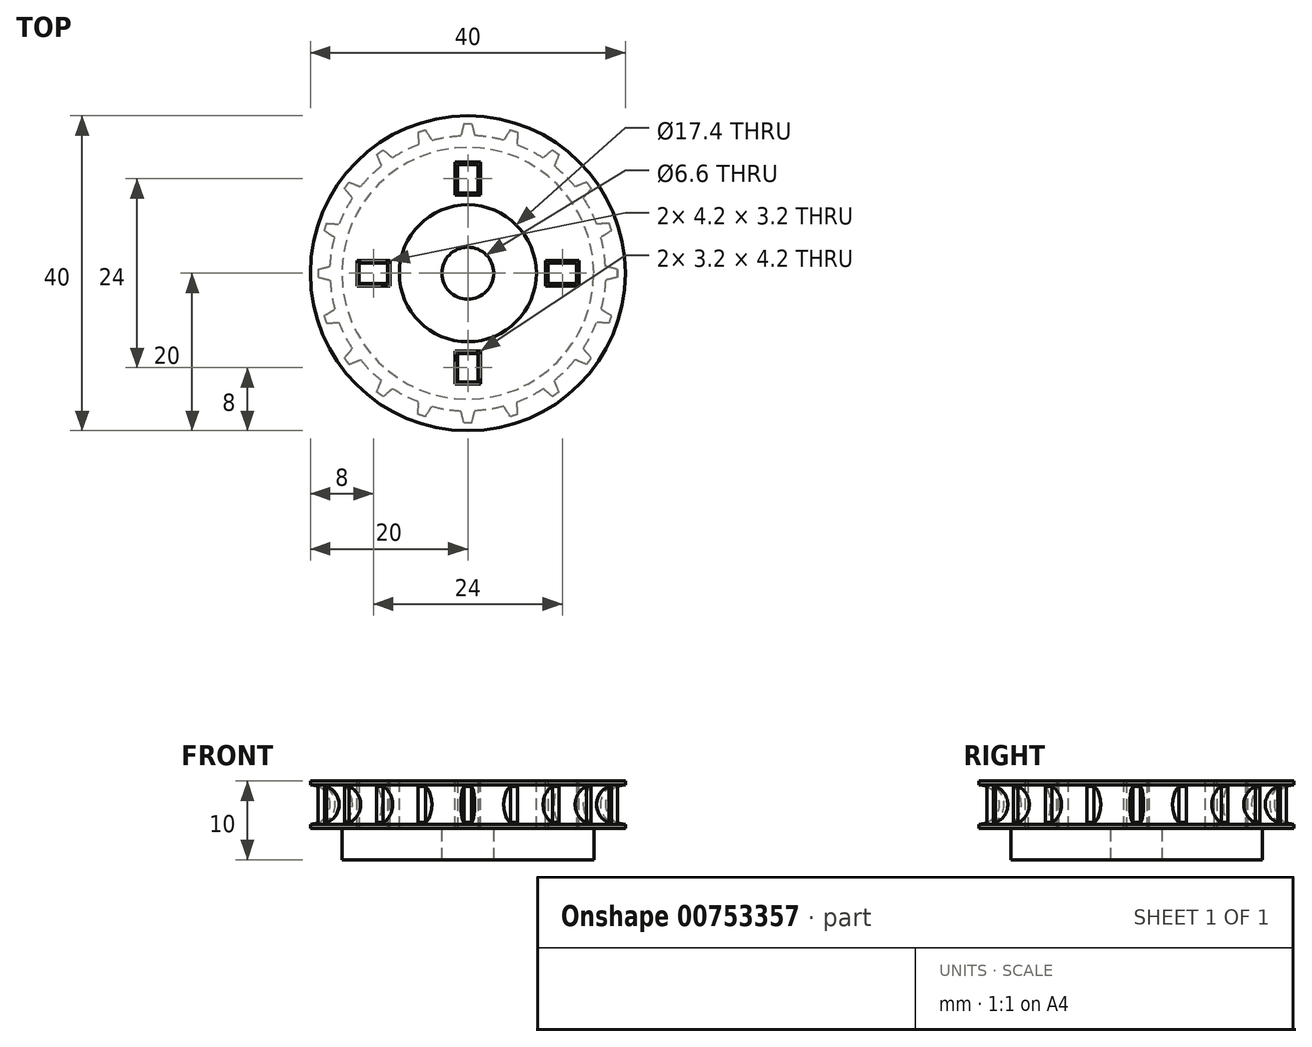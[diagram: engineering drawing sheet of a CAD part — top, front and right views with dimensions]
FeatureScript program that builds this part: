
annotation { "Feature Type Name" : "Feature", "Feature Type Description" : "" }
export const myFeature = defineFeature(function(context is Context, id is Id, definition is map)
    precondition{}
    {
        {
            var Q0;
            Q0=qCreatedBy(makeId("Right.planeOp"),FACE);
            var sketch = newSketch(context, id + "F0", { "sketchPlane" : qUnion([Q0])});
            skLineSegment(sketch, "E0", {"start": v(0, 6) * mm, "end": v(-20, 6) * mm});
            skLineSegment(sketch, "E1", {"start": v(-20, 5.5) * mm, "end": v(-20, 6) * mm});
            skLineSegment(sketch, "E2", {"start": v(-20, 0.5) * mm, "end": v(-20, 0) * mm});
            skArc(sketch, "E3", {"start": v(-20, 0.5) * mm, "mid": v(-17.5, 3) * mm, "end": v(-20, 5.5) * mm});
            skLineSegment(sketch, "E4", {"start": v(0, 6) * mm, "end": v(0, 0) * mm});
            skLineSegment(sketch, "E5", {"start": v(0, -4) * mm, "end": v(0, 0) * mm});
            skLineSegment(sketch, "E6", {"start": v(0, -4) * mm, "end": v(-16, -4) * mm});
            skLineSegment(sketch, "E7", {"start": v(-16, -4) * mm, "end": v(-16, 0) * mm});
            skLineSegment(sketch, "E8", {"start": v(-16, 0) * mm, "end": v(-20, 0) * mm});
            skLineSegment(sketch, "E9", {"start": v(-16, 0) * mm, "end": v(0, 0) * mm});
            skSolve(sketch);
        }
        {
            var Q0;
            Q0=makeQuery(id+"F0.imprint","IMPRINT",FACE,{"disambiguationData":[TD([[makeQuery(id+"F0.imprint","IMPRINT",EDGE,{"derivedFrom":sQuery(id+"F0.wireOp",EDGE,"E0")}),1.0]])]});
            var Q1;
            Q1=sQuery(id+"F0.wireOp",EDGE,"E4");
            revolve(context, id + "F1", {"surfaceOperationType" : NewSurfaceOperationType.NEW, "entities" : qUnion([Q0]), "axis" : qUnion([Q1]), "revolveType" : RevolveType.FULL});
        }
        {
            var Q0;
            Q0=makeQuery(id+"F1.opRevolve","SWEPT_FACE",FACE,{"disambiguationData":[OSD([sQuery(id+"F0.wireOp",EDGE,"E0")])]});
            var sketch = newSketch(context, id + "F2", { "sketchPlane" : qUnion([Q0])});
            skLineSegment(sketch, "E10", {"start": v(-17, 1) * mm, "end": v(-17, 0) * mm});
            skLineSegment(sketch, "E11", {"start": v(-17, 0) * mm, "end": v(-17, -1) * mm});
            skLineSegment(sketch, "E12", {"start": v(-17, -1) * mm, "end": v(-19, -0.5) * mm});
            skLineSegment(sketch, "E13", {"start": v(-19, -0.5) * mm, "end": v(-19, 0.5) * mm});
            skLineSegment(sketch, "E14", {"start": v(-19, 0.5) * mm, "end": v(-17, 1) * mm});
            skPoint(sketch, "E15", {"position": v(0, 0) * mm});
            skLineSegment(sketch, "E16", {"start": v(0, 9.9) * mm, "end": v(1.6, 9.9) * mm});
            skLineSegment(sketch, "E17", {"start": v(1.6, 9.9) * mm, "end": v(1.6, 14.1) * mm});
            skLineSegment(sketch, "E18", {"start": v(1.6, 14.1) * mm, "end": v(-1.6, 14.1) * mm});
            skLineSegment(sketch, "E19", {"start": v(0, 9.9) * mm, "end": v(-1.6, 9.9) * mm});
            skLineSegment(sketch, "E20", {"start": v(-1.6, 9.9) * mm, "end": v(-1.6, 14.1) * mm});
            skLineSegment(sketch, "E21.1.0", {"start": v(-18.22, -5.4) * mm, "end": v(-16.48, -4.3) * mm});
            skLineSegment(sketch, "E21.1.1", {"start": v(-15.86, -6.2) * mm, "end": v(-17.92, -6.35) * mm});
            skLineSegment(sketch, "E21.1.2", {"start": v(-17.92, -6.35) * mm, "end": v(-18.22, -5.4) * mm});
            skLineSegment(sketch, "E21.1.3", {"start": v(-16.17, -5.25) * mm, "end": v(-15.86, -6.2) * mm});
            skLineSegment(sketch, "E21.1.4", {"start": v(-16.48, -4.3) * mm, "end": v(-16.17, -5.25) * mm});
            skLineSegment(sketch, "E21.2.0", {"start": v(-15.67, -10.76) * mm, "end": v(-14.34, -9.18) * mm});
            skLineSegment(sketch, "E21.2.1", {"start": v(-13.17, -10.8) * mm, "end": v(-15.08, -11.57) * mm});
            skLineSegment(sketch, "E21.2.2", {"start": v(-15.08, -11.57) * mm, "end": v(-15.67, -10.76) * mm});
            skLineSegment(sketch, "E21.2.3", {"start": v(-13.75, -10) * mm, "end": v(-13.17, -10.8) * mm});
            skLineSegment(sketch, "E21.2.4", {"start": v(-14.34, -9.18) * mm, "end": v(-13.75, -10) * mm});
            skLineSegment(sketch, "E21.3.0", {"start": v(-11.57, -15.08) * mm, "end": v(-10.8, -13.17) * mm});
            skLineSegment(sketch, "E21.3.1", {"start": v(-9.18, -14.34) * mm, "end": v(-10.76, -15.67) * mm});
            skLineSegment(sketch, "E21.3.2", {"start": v(-10.76, -15.67) * mm, "end": v(-11.57, -15.08) * mm});
            skLineSegment(sketch, "E21.3.3", {"start": v(-10, -13.75) * mm, "end": v(-9.18, -14.34) * mm});
            skLineSegment(sketch, "E21.3.4", {"start": v(-10.8, -13.17) * mm, "end": v(-10, -13.75) * mm});
            skLineSegment(sketch, "E21.4.0", {"start": v(-6.35, -17.92) * mm, "end": v(-6.2, -15.86) * mm});
            skLineSegment(sketch, "E21.4.1", {"start": v(-4.3, -16.48) * mm, "end": v(-5.4, -18.22) * mm});
            skLineSegment(sketch, "E21.4.2", {"start": v(-5.4, -18.22) * mm, "end": v(-6.35, -17.92) * mm});
            skLineSegment(sketch, "E21.4.3", {"start": v(-5.25, -16.17) * mm, "end": v(-4.3, -16.48) * mm});
            skLineSegment(sketch, "E21.4.4", {"start": v(-6.2, -15.86) * mm, "end": v(-5.25, -16.17) * mm});
            skLineSegment(sketch, "E21.5.0", {"start": v(-0.5, -19) * mm, "end": v(-1, -17) * mm});
            skLineSegment(sketch, "E21.5.1", {"start": v(1, -17) * mm, "end": v(0.5, -19) * mm});
            skLineSegment(sketch, "E21.5.2", {"start": v(0.5, -19) * mm, "end": v(-0.5, -19) * mm});
            skLineSegment(sketch, "E21.5.3", {"start": v(0, -17) * mm, "end": v(1, -17) * mm});
            skLineSegment(sketch, "E21.5.4", {"start": v(-1, -17) * mm, "end": v(0, -17) * mm});
            skLineSegment(sketch, "E21.6.0", {"start": v(5.4, -18.22) * mm, "end": v(4.3, -16.48) * mm});
            skLineSegment(sketch, "E21.6.1", {"start": v(6.2, -15.86) * mm, "end": v(6.35, -17.92) * mm});
            skLineSegment(sketch, "E21.6.2", {"start": v(6.35, -17.92) * mm, "end": v(5.4, -18.22) * mm});
            skLineSegment(sketch, "E21.6.3", {"start": v(5.25, -16.17) * mm, "end": v(6.2, -15.86) * mm});
            skLineSegment(sketch, "E21.6.4", {"start": v(4.3, -16.48) * mm, "end": v(5.25, -16.17) * mm});
            skLineSegment(sketch, "E21.7.0", {"start": v(10.76, -15.67) * mm, "end": v(9.18, -14.34) * mm});
            skLineSegment(sketch, "E21.7.1", {"start": v(10.8, -13.17) * mm, "end": v(11.57, -15.08) * mm});
            skLineSegment(sketch, "E21.7.2", {"start": v(11.57, -15.08) * mm, "end": v(10.76, -15.67) * mm});
            skLineSegment(sketch, "E21.7.3", {"start": v(10, -13.75) * mm, "end": v(10.8, -13.17) * mm});
            skLineSegment(sketch, "E21.7.4", {"start": v(9.18, -14.34) * mm, "end": v(10, -13.75) * mm});
            skLineSegment(sketch, "E21.8.0", {"start": v(15.08, -11.57) * mm, "end": v(13.17, -10.8) * mm});
            skLineSegment(sketch, "E21.8.1", {"start": v(14.34, -9.18) * mm, "end": v(15.67, -10.76) * mm});
            skLineSegment(sketch, "E21.8.2", {"start": v(15.67, -10.76) * mm, "end": v(15.08, -11.57) * mm});
            skLineSegment(sketch, "E21.8.3", {"start": v(13.75, -10) * mm, "end": v(14.34, -9.18) * mm});
            skLineSegment(sketch, "E21.8.4", {"start": v(13.17, -10.8) * mm, "end": v(13.75, -10) * mm});
            skLineSegment(sketch, "E21.9.0", {"start": v(17.92, -6.35) * mm, "end": v(15.86, -6.2) * mm});
            skLineSegment(sketch, "E21.9.1", {"start": v(16.48, -4.3) * mm, "end": v(18.22, -5.4) * mm});
            skLineSegment(sketch, "E21.9.2", {"start": v(18.22, -5.4) * mm, "end": v(17.92, -6.35) * mm});
            skLineSegment(sketch, "E21.9.3", {"start": v(16.17, -5.25) * mm, "end": v(16.48, -4.3) * mm});
            skLineSegment(sketch, "E21.9.4", {"start": v(15.86, -6.2) * mm, "end": v(16.17, -5.25) * mm});
            skLineSegment(sketch, "E21.10.0", {"start": v(19, -0.5) * mm, "end": v(17, -1) * mm});
            skLineSegment(sketch, "E21.10.1", {"start": v(17, 1) * mm, "end": v(19, 0.5) * mm});
            skLineSegment(sketch, "E21.10.2", {"start": v(19, 0.5) * mm, "end": v(19, -0.5) * mm});
            skLineSegment(sketch, "E21.10.3", {"start": v(17, 0) * mm, "end": v(17, 1) * mm});
            skLineSegment(sketch, "E21.10.4", {"start": v(17, -1) * mm, "end": v(17, 0) * mm});
            skLineSegment(sketch, "E21.11.0", {"start": v(18.22, 5.4) * mm, "end": v(16.48, 4.3) * mm});
            skLineSegment(sketch, "E21.11.1", {"start": v(15.86, 6.2) * mm, "end": v(17.92, 6.35) * mm});
            skLineSegment(sketch, "E21.11.2", {"start": v(17.92, 6.35) * mm, "end": v(18.22, 5.4) * mm});
            skLineSegment(sketch, "E21.11.3", {"start": v(16.17, 5.25) * mm, "end": v(15.86, 6.2) * mm});
            skLineSegment(sketch, "E21.11.4", {"start": v(16.48, 4.3) * mm, "end": v(16.17, 5.25) * mm});
            skLineSegment(sketch, "E21.12.0", {"start": v(15.67, 10.76) * mm, "end": v(14.34, 9.18) * mm});
            skLineSegment(sketch, "E21.12.1", {"start": v(13.17, 10.8) * mm, "end": v(15.08, 11.57) * mm});
            skLineSegment(sketch, "E21.12.2", {"start": v(15.08, 11.57) * mm, "end": v(15.67, 10.76) * mm});
            skLineSegment(sketch, "E21.12.3", {"start": v(13.75, 10) * mm, "end": v(13.17, 10.8) * mm});
            skLineSegment(sketch, "E21.12.4", {"start": v(14.34, 9.18) * mm, "end": v(13.75, 10) * mm});
            skLineSegment(sketch, "E21.13.0", {"start": v(11.57, 15.08) * mm, "end": v(10.8, 13.17) * mm});
            skLineSegment(sketch, "E21.13.1", {"start": v(9.18, 14.34) * mm, "end": v(10.76, 15.67) * mm});
            skLineSegment(sketch, "E21.13.2", {"start": v(10.76, 15.67) * mm, "end": v(11.57, 15.08) * mm});
            skLineSegment(sketch, "E21.13.3", {"start": v(10, 13.75) * mm, "end": v(9.18, 14.34) * mm});
            skLineSegment(sketch, "E21.13.4", {"start": v(10.8, 13.17) * mm, "end": v(10, 13.75) * mm});
            skLineSegment(sketch, "E21.14.0", {"start": v(6.35, 17.92) * mm, "end": v(6.2, 15.86) * mm});
            skLineSegment(sketch, "E21.14.1", {"start": v(4.3, 16.48) * mm, "end": v(5.4, 18.22) * mm});
            skLineSegment(sketch, "E21.14.2", {"start": v(5.4, 18.22) * mm, "end": v(6.35, 17.92) * mm});
            skLineSegment(sketch, "E21.14.3", {"start": v(5.25, 16.17) * mm, "end": v(4.3, 16.48) * mm});
            skLineSegment(sketch, "E21.14.4", {"start": v(6.2, 15.86) * mm, "end": v(5.25, 16.17) * mm});
            skLineSegment(sketch, "E21.15.0", {"start": v(0.5, 19) * mm, "end": v(1, 17) * mm});
            skLineSegment(sketch, "E21.15.1", {"start": v(-1, 17) * mm, "end": v(-0.5, 19) * mm});
            skLineSegment(sketch, "E21.15.2", {"start": v(-0.5, 19) * mm, "end": v(0.5, 19) * mm});
            skLineSegment(sketch, "E21.15.3", {"start": v(0, 17) * mm, "end": v(-1, 17) * mm});
            skLineSegment(sketch, "E21.15.4", {"start": v(1, 17) * mm, "end": v(0, 17) * mm});
            skLineSegment(sketch, "E21.16.0", {"start": v(-5.4, 18.22) * mm, "end": v(-4.3, 16.48) * mm});
            skLineSegment(sketch, "E21.16.1", {"start": v(-6.2, 15.86) * mm, "end": v(-6.35, 17.92) * mm});
            skLineSegment(sketch, "E21.16.2", {"start": v(-6.35, 17.92) * mm, "end": v(-5.4, 18.22) * mm});
            skLineSegment(sketch, "E21.16.3", {"start": v(-5.25, 16.17) * mm, "end": v(-6.2, 15.86) * mm});
            skLineSegment(sketch, "E21.16.4", {"start": v(-4.3, 16.48) * mm, "end": v(-5.25, 16.17) * mm});
            skLineSegment(sketch, "E21.17.0", {"start": v(-10.76, 15.67) * mm, "end": v(-9.18, 14.34) * mm});
            skLineSegment(sketch, "E21.17.1", {"start": v(-10.8, 13.17) * mm, "end": v(-11.57, 15.08) * mm});
            skLineSegment(sketch, "E21.17.2", {"start": v(-11.57, 15.08) * mm, "end": v(-10.76, 15.67) * mm});
            skLineSegment(sketch, "E21.17.3", {"start": v(-10, 13.75) * mm, "end": v(-10.8, 13.17) * mm});
            skLineSegment(sketch, "E21.17.4", {"start": v(-9.18, 14.34) * mm, "end": v(-10, 13.75) * mm});
            skLineSegment(sketch, "E21.18.0", {"start": v(-15.08, 11.57) * mm, "end": v(-13.17, 10.8) * mm});
            skLineSegment(sketch, "E21.18.1", {"start": v(-14.34, 9.18) * mm, "end": v(-15.67, 10.76) * mm});
            skLineSegment(sketch, "E21.18.2", {"start": v(-15.67, 10.76) * mm, "end": v(-15.08, 11.57) * mm});
            skLineSegment(sketch, "E21.18.3", {"start": v(-13.75, 10) * mm, "end": v(-14.34, 9.18) * mm});
            skLineSegment(sketch, "E21.18.4", {"start": v(-13.17, 10.8) * mm, "end": v(-13.75, 10) * mm});
            skLineSegment(sketch, "E21.19.0", {"start": v(-17.92, 6.35) * mm, "end": v(-15.86, 6.2) * mm});
            skLineSegment(sketch, "E21.19.1", {"start": v(-16.48, 4.3) * mm, "end": v(-18.22, 5.4) * mm});
            skLineSegment(sketch, "E21.19.2", {"start": v(-18.22, 5.4) * mm, "end": v(-17.92, 6.35) * mm});
            skLineSegment(sketch, "E21.19.3", {"start": v(-16.17, 5.25) * mm, "end": v(-16.48, 4.3) * mm});
            skLineSegment(sketch, "E21.19.4", {"start": v(-15.86, 6.2) * mm, "end": v(-16.17, 5.25) * mm});
            skPoint(sketch, "E22.center", {"position": v(0.05, 0.05) * mm});
            skLineSegment(sketch, "E23.1.0", {"start": v(-9.9, 0) * mm, "end": v(-9.9, 1.6) * mm});
            skLineSegment(sketch, "E23.1.1", {"start": v(-9.9, 1.6) * mm, "end": v(-14.1, 1.6) * mm});
            skLineSegment(sketch, "E23.1.2", {"start": v(-9.9, -1.6) * mm, "end": v(-14.1, -1.6) * mm});
            skLineSegment(sketch, "E23.1.3", {"start": v(-9.9, 0) * mm, "end": v(-9.9, -1.6) * mm});
            skLineSegment(sketch, "E23.1.4", {"start": v(-14.1, 1.6) * mm, "end": v(-14.1, -1.6) * mm});
            skLineSegment(sketch, "E23.2.0", {"start": v(0, -9.9) * mm, "end": v(-1.6, -9.9) * mm});
            skLineSegment(sketch, "E23.2.1", {"start": v(-1.6, -9.9) * mm, "end": v(-1.6, -14.1) * mm});
            skLineSegment(sketch, "E23.2.2", {"start": v(1.6, -9.9) * mm, "end": v(1.6, -14.1) * mm});
            skLineSegment(sketch, "E23.2.3", {"start": v(0, -9.9) * mm, "end": v(1.6, -9.9) * mm});
            skLineSegment(sketch, "E23.2.4", {"start": v(-1.6, -14.1) * mm, "end": v(1.6, -14.1) * mm});
            skLineSegment(sketch, "E23.3.0", {"start": v(9.9, 0) * mm, "end": v(9.9, -1.6) * mm});
            skLineSegment(sketch, "E23.3.1", {"start": v(9.9, -1.6) * mm, "end": v(14.1, -1.6) * mm});
            skLineSegment(sketch, "E23.3.2", {"start": v(9.9, 1.6) * mm, "end": v(14.1, 1.6) * mm});
            skLineSegment(sketch, "E23.3.3", {"start": v(9.9, 0) * mm, "end": v(9.9, 1.6) * mm});
            skLineSegment(sketch, "E23.3.4", {"start": v(14.1, -1.6) * mm, "end": v(14.1, 1.6) * mm});
            skSolve(sketch);
        }
        {
            var Q0;
            Q0=qSketchRegion(id+"F2",true);
            extrude(context, id + "F3", {"entities" : qUnion([Q0]), "operationType" : NewBodyOperationType.ADD, "oppositeDirection" : true, "depth" : 6 * mm, "offsetDistance" : 25 * mm});
        }
        {
            var Q0;
            Q0=makeQuery(id+"F2.imprint","IMPRINT",FACE,{"disambiguationData":[TD([[makeQuery(id+"F2.imprint","IMPRINT",EDGE,{"derivedFrom":sQuery(id+"F2.wireOp",EDGE,"E16")}),1.0]])]});
            var Q1;
            Q1=makeQuery(id+"F2.imprint","IMPRINT",FACE,{"disambiguationData":[TD([[makeQuery(id+"F2.imprint","IMPRINT",EDGE,{"derivedFrom":sQuery(id+"F2.wireOp",EDGE,"E23.3.0")}),1.0]])]});
            var Q2;
            Q2=makeQuery(id+"F2.imprint","IMPRINT",FACE,{"disambiguationData":[TD([[makeQuery(id+"F2.imprint","IMPRINT",EDGE,{"derivedFrom":sQuery(id+"F2.wireOp",EDGE,"E23.2.0")}),1.0]])]});
            var Q3;
            Q3=makeQuery(id+"F2.imprint","IMPRINT",FACE,{"disambiguationData":[TD([[makeQuery(id+"F2.imprint","IMPRINT",EDGE,{"derivedFrom":sQuery(id+"F2.wireOp",EDGE,"E23.1.0")}),1.0]])]});
            extrude(context, id + "F4", {"entities" : qUnion([Q0, Q1, Q2, Q3]), "operationType" : NewBodyOperationType.REMOVE, "oppositeDirection" : true, "depth" : 25 * mm, "offsetDistance" : 25 * mm});
        }
        {
            var Q0;
            Q0=sQuery(id+"F2.wireOp",VERTEX,"E15");
            var Q1;
            Q1=makeQuery(id+"F1.opRevolve","SWEPT_BODY",BODY,{"disambiguationData":[OSD([sQuery(id+"F0.wireOp",EDGE,"0uZ5v6Zf-e6fI-ENXi-FmPJ-4enIQuWO969C"),sQuery(id+"F0.wireOp",EDGE,"Bkx8NRw9-TRud-6wcE-ZtgN-uS6PIwQ9x0rI"),sQuery(id+"F0.wireOp",EDGE,"qVFkTcKz-0Ocm-P27z-k9Ir-7DMV1ABQbCdZ"),sQuery(id+"F0.wireOp",EDGE,"E0"),sQuery(id+"F0.wireOp",EDGE,"IEXSFwqa-9eCT-NjnN-pBMk-4ELdBoPE1w2z"),sQuery(id+"F0.wireOp",EDGE,"E1"),sQuery(id+"F0.wireOp",EDGE,"E2"),sQuery(id+"F0.wireOp",EDGE,"E3")])]});
            hole(context, id + "F5", {"style" : HoleStyle.C_BORE, "endStyle" : HoleEndStyle.THROUGH, "holeDiameter" : 6.6 * mm, "cBoreDiameter" : 17.4 * mm, "cBoreDepth" : 6 * mm, "majorDiameter" : 5 * mm, "isTappedThrough" : true, "tappedDepth" : 12 * mm, "tapClearance" : 3, "locations" : qUnion([Q0]), "scope" : qUnion([Q1])});
        }
        {
            var Q0;
            Q0=makeQuery(id+"F0.imprint","IMPRINT",FACE,{"disambiguationData":[TD([[makeQuery(id+"F0.imprint","IMPRINT",EDGE,{"derivedFrom":sQuery(id+"F0.wireOp",EDGE,"E5")}),1.0]])]});
            var Q1;
            Q1=sQuery(id+"F0.wireOp",EDGE,"E5");
            revolve(context, id + "F6", {"surfaceOperationType" : NewSurfaceOperationType.NEW, "entities" : qUnion([Q0]), "axis" : qUnion([Q1]), "revolveType" : RevolveType.FULL});
        }
        {
            var Q0;
            Q0=makeQuery(id+"F6.opRevolve","SWEPT_FACE",FACE,{"disambiguationData":[OSD([sQuery(id+"F0.wireOp",EDGE,"E9")])]});
            var sketch = newSketch(context, id + "F7", { "sketchPlane" : qUnion([Q0])});
            skLineSegment(sketch, "E24.bottom", {"start": v(-1.3, 13.8) * mm, "end": v(1.3, 13.8) * mm});
            skLineSegment(sketch, "E24.left", {"start": v(-1.3, 13.8) * mm, "end": v(-1.3, 10.2) * mm});
            skLineSegment(sketch, "E24.right", {"start": v(1.3, 13.8) * mm, "end": v(1.3, 10.2) * mm});
            skLineSegment(sketch, "E25", {"start": v(-1.3, 10.2) * mm, "end": v(0, 10.2) * mm});
            skLineSegment(sketch, "E26", {"start": v(0, 10.2) * mm, "end": v(1.3, 10.2) * mm});
            skLineSegment(sketch, "E27.1.0", {"start": v(-13.8, 1.3) * mm, "end": v(-10.2, 1.3) * mm});
            skLineSegment(sketch, "E27.1.1", {"start": v(-13.8, -1.3) * mm, "end": v(-10.2, -1.3) * mm});
            skLineSegment(sketch, "E27.1.2", {"start": v(-10.2, 0) * mm, "end": v(-10.2, 1.3) * mm});
            skLineSegment(sketch, "E27.1.3", {"start": v(-13.8, -1.3) * mm, "end": v(-13.8, 1.3) * mm});
            skLineSegment(sketch, "E27.1.4", {"start": v(-10.2, -1.3) * mm, "end": v(-10.2, 0) * mm});
            skLineSegment(sketch, "E27.2.0", {"start": v(-1.3, -13.8) * mm, "end": v(-1.3, -10.2) * mm});
            skLineSegment(sketch, "E27.2.1", {"start": v(1.3, -13.8) * mm, "end": v(1.3, -10.2) * mm});
            skLineSegment(sketch, "E27.2.2", {"start": v(0, -10.2) * mm, "end": v(-1.3, -10.2) * mm});
            skLineSegment(sketch, "E27.2.3", {"start": v(1.3, -13.8) * mm, "end": v(-1.3, -13.8) * mm});
            skLineSegment(sketch, "E27.2.4", {"start": v(1.3, -10.2) * mm, "end": v(0, -10.2) * mm});
            skLineSegment(sketch, "E27.3.0", {"start": v(13.8, -1.3) * mm, "end": v(10.2, -1.3) * mm});
            skLineSegment(sketch, "E27.3.1", {"start": v(13.8, 1.3) * mm, "end": v(10.2, 1.3) * mm});
            skLineSegment(sketch, "E27.3.2", {"start": v(10.2, 0) * mm, "end": v(10.2, -1.3) * mm});
            skLineSegment(sketch, "E27.3.3", {"start": v(13.8, 1.3) * mm, "end": v(13.8, -1.3) * mm});
            skLineSegment(sketch, "E27.3.4", {"start": v(10.2, 1.3) * mm, "end": v(10.2, 0) * mm});
            skPoint(sketch, "E27.center", {"position": v(0, 0) * mm});
            skSolve(sketch);
        }
        {
            var Q0;
            Q0 = qSketchRegion(id + "F7", true);
            extrude(context, id + "F8", {"entities" : qUnion([Q0]), "operationType" : NewBodyOperationType.ADD, "depth" : 6 * mm, "offsetDistance" : 25 * mm});
        }
        {
            var Q0;
            Q0=sQuery(id+"F2.wireOp",VERTEX,"E15");
            var Q1;
            Q1=makeQuery(id+"F6.opRevolve","SWEPT_BODY",BODY,{"disambiguationData":[OSD([sQuery(id+"F0.wireOp",EDGE,"b9zqWd5P-BOSM-oKXY-fWpn-oY6lwcDiA7It"),sQuery(id+"F0.wireOp",EDGE,"z89z02PJ-dX0P-rekZ-uTto-VWizik7Fe6uF"),sQuery(id+"F0.wireOp",EDGE,"ySgeQPn5-eQBZ-eF80-W9g7-QtHDcXMWjfkX"),sQuery(id+"F0.wireOp",EDGE,"E5")])]});
            hole(context, id + "F9", {"style" : HoleStyle.SIMPLE, "endStyle" : HoleEndStyle.THROUGH, "standardTappedOrClearance" : lookupTablePath({ "fit" : "Normal", "standard" : "ISO", "size" : "M6", "type" : "Clearance" }), "standardBlindInLast" : lookupTablePath({ "fit" : "Standard", "standard" : "ISO", "size" : "M6", "type" : "Clearance" }), "holeDiameter" : 6.6 * mm, "majorDiameter" : 5 * mm, "isTappedThrough" : true, "tappedDepth" : 12 * mm, "tapClearance" : 3, "locations" : qUnion([Q0]), "scope" : qUnion([Q1])});
        }
    });
